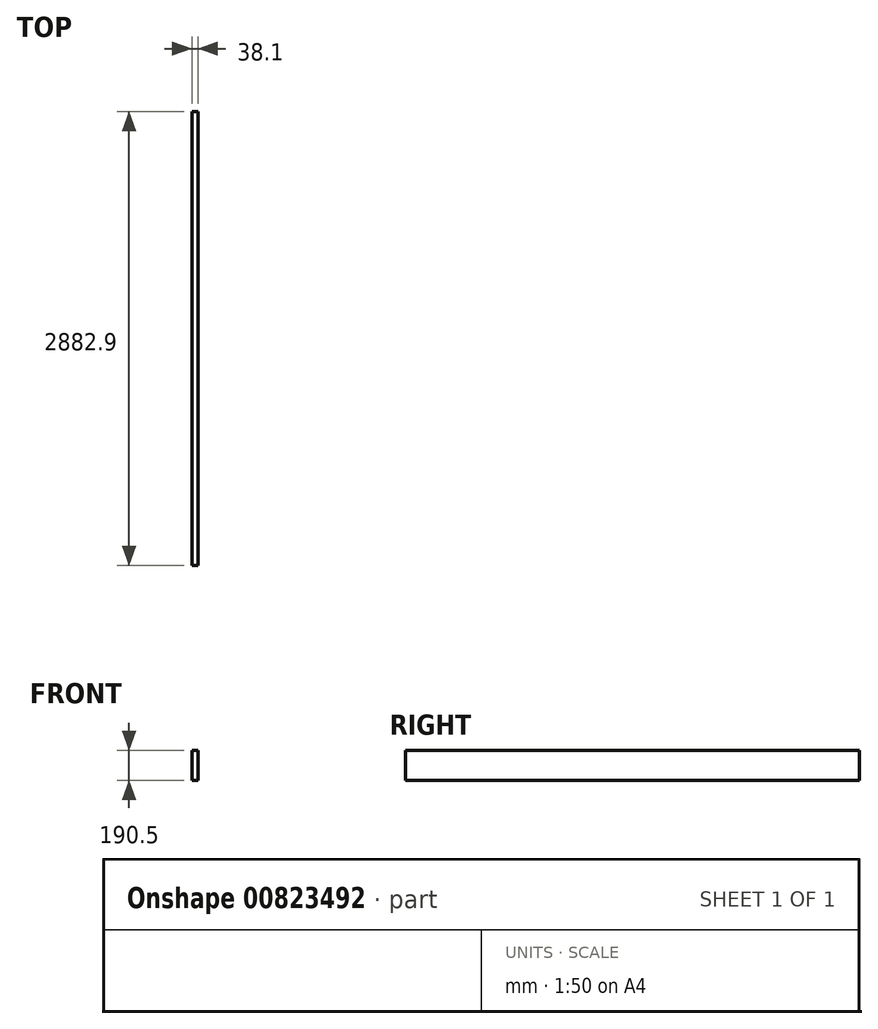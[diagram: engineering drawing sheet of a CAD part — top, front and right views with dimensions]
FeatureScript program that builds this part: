
annotation { "Feature Type Name" : "Feature", "Feature Type Description" : "" }
export const myFeature = defineFeature(function(context is Context, id is Id, definition is map)
    precondition{}
    {
        {
            var Q0;
            Q0=qCreatedBy(makeId("Front.planeOp"),FACE);
            var sketch = newSketch(context, id + "F0", { "sketchPlane" : qUnion([Q0])});
            skLineSegment(sketch, "E0.bottom", {"start": v(0, 0) * mm, "end": v(38.1, 0) * mm});
            skLineSegment(sketch, "E0.top", {"start": v(0, 190.5) * mm, "end": v(38.1, 190.5) * mm});
            skLineSegment(sketch, "E0.left", {"start": v(0, 0) * mm, "end": v(0, 190.5) * mm});
            skLineSegment(sketch, "E0.right", {"start": v(38.1, 0) * mm, "end": v(38.1, 190.5) * mm});
            skSolve(sketch);
        }
        {
            var Q0;
            Q0=qSketchRegion(id+"F0",true);
            extrude(context, id + "F1", {"entities" : qUnion([Q0]), "depth" : 2882.9 * mm, "offsetDistance" : 25.4 * mm});
        }
    });
